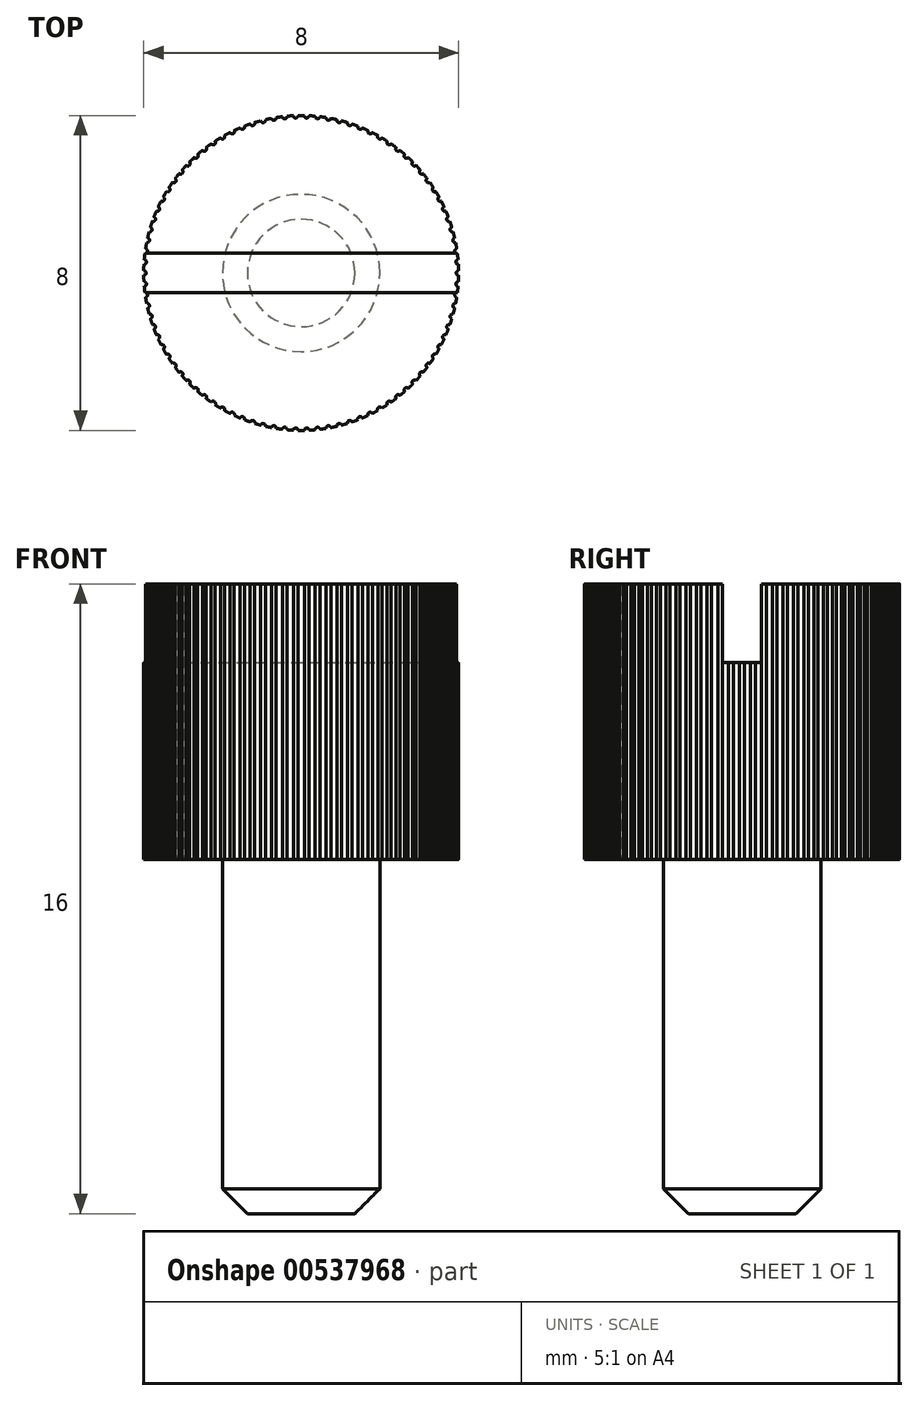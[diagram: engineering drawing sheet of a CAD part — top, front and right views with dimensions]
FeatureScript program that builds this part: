
annotation { "Feature Type Name" : "Feature", "Feature Type Description" : "" }
export const myFeature = defineFeature(function(context is Context, id is Id, definition is map)
    precondition{}
    {
        {
            var Q0;
            Q0=qCreatedBy(makeId("Top.planeOp"),FACE);
            var sketch = newSketch(context, id + "F0", { "sketchPlane" : qUnion([Q0])});
            skCircle(sketch, "E0", {"center": v(0, 0) * mm, "radius": 2 * mm});
            skSolve(sketch);
        }
        {
            var Q0;
            Q0=makeQuery(id+"F0.imprint","IMPRINT",FACE,{"disambiguationData":[TD([[makeQuery(id+"F0.imprint","IMPRINT",EDGE,{"derivedFrom":sQuery(id+"F0.wireOp",EDGE,"E0")}),1.0]])]});
            extrude(context, id + "F1", {"entities" : qUnion([Q0]), "oppositeDirection" : true, "depth" : 9 * mm, "offsetDistance" : 25 * mm});
        }
        {
            var Q0;
            Q0=qCreatedBy(makeId("Top.planeOp"),FACE);
            var sketch = newSketch(context, id + "F2", { "sketchPlane" : qUnion([Q0])});
            skCircle(sketch, "E1", {"center": v(0, 0) * mm, "radius": 4 * mm});
            skSolve(sketch);
        }
        {
            var Q0;
            Q0=makeQuery(id+"F2.imprint","IMPRINT",FACE,{"disambiguationData":[TD([[makeQuery(id+"F2.imprint","IMPRINT",EDGE,{"derivedFrom":sQuery(id+"F2.wireOp",EDGE,"E1")}),1.0]])]});
            extrude(context, id + "F3", {"entities" : qUnion([Q0]), "operationType" : NewBodyOperationType.ADD, "depth" : 7 * mm, "offsetDistance" : 25 * mm});
        }
        {
            var Q0;
            Q0=makeQuery(id+"F3.opExtrude","CAP_FACE",FACE,{"disambiguationData":[OSD([sQuery(id+"F2.wireOp",EDGE,"E1")])],"isStart":false});
            var sketch = newSketch(context, id + "F4", { "sketchPlane" : qUnion([Q0])});
            skLineSegment(sketch, "E2.bottom", {"start": v(-4.5, 0.5) * mm, "end": v(4.5, 0.5) * mm});
            skLineSegment(sketch, "E2.top", {"start": v(-4.5, -0.5) * mm, "end": v(4.5, -0.5) * mm});
            skLineSegment(sketch, "E2.left", {"start": v(-4.5, 0.5) * mm, "end": v(-4.5, -0.5) * mm});
            skLineSegment(sketch, "E2.right", {"start": v(4.5, 0.5) * mm, "end": v(4.5, -0.5) * mm});
            skPoint(sketch, "E2.middle", {"position": v(0, 0) * mm});
            skSolve(sketch);
        }
        {
            var Q0;
            Q0=qSketchRegion(id+"F4",true);
            extrude(context, id + "F5", {"entities" : qUnion([Q0]), "operationType" : NewBodyOperationType.REMOVE, "oppositeDirection" : true, "depth" : 2 * mm, "offsetDistance" : 25 * mm});
        }
        {
            var Q0;
            Q0=makeQuery(id+"F1.opExtrude","CAP_EDGE",EDGE,{"disambiguationData":[OSD([sQuery(id+"F0.wireOp",EDGE,"E0")])],"isStart":false});
            chamfer(context, id + "F6", {"entities" : qUnion([Q0]), "width" : .635 * mm, "tangentPropagation" : true});
        }
        {
            var Q0;
            Q0=makeQuery(id+"F3.opExtrude","CAP_FACE",FACE,{"disambiguationData":[OSD([sQuery(id+"F2.wireOp",EDGE,"E1")])],"isStart":true});
            var sketch = newSketch(context, id + "F7", { "sketchPlane" : qUnion([Q0])});
            skPoint(sketch, "E3", {"position": v(4, 0) * mm});
            skPoint(sketch, "E4.1.0", {"position": v(4, 0.28) * mm});
            skPoint(sketch, "E4.2.0", {"position": v(3.96, 0.56) * mm});
            skPoint(sketch, "E4.3.0", {"position": v(3.91, 0.83) * mm});
            skPoint(sketch, "E4.4.0", {"position": v(3.85, 1.1) * mm});
            skPoint(sketch, "E4.5.0", {"position": v(3.76, 1.37) * mm});
            skPoint(sketch, "E4.6.0", {"position": v(3.65, 1.63) * mm});
            skPoint(sketch, "E4.7.0", {"position": v(3.53, 1.88) * mm});
            skPoint(sketch, "E4.8.0", {"position": v(3.4, 2.12) * mm});
            skPoint(sketch, "E4.9.0", {"position": v(3.24, 2.35) * mm});
            skPoint(sketch, "E4.10.0", {"position": v(3.06, 2.57) * mm});
            skPoint(sketch, "E4.11.0", {"position": v(2.88, 2.78) * mm});
            skPoint(sketch, "E4.12.0", {"position": v(2.68, 2.97) * mm});
            skPoint(sketch, "E4.13.0", {"position": v(2.46, 3.15) * mm});
            skPoint(sketch, "E4.14.0", {"position": v(2.24, 3.32) * mm});
            skPoint(sketch, "E4.15.0", {"position": v(2, 3.46) * mm});
            skPoint(sketch, "E4.16.0", {"position": v(1.75, 3.6) * mm});
            skPoint(sketch, "E4.17.0", {"position": v(1.5, 3.7) * mm});
            skPoint(sketch, "E4.18.0", {"position": v(1.24, 3.8) * mm});
            skPoint(sketch, "E4.19.0", {"position": v(0.97, 3.88) * mm});
            skPoint(sketch, "E4.20.0", {"position": v(0.7, 3.94) * mm});
            skPoint(sketch, "E4.21.0", {"position": v(0.42, 3.98) * mm});
            skPoint(sketch, "E4.22.0", {"position": v(0.14, 4) * mm});
            skPoint(sketch, "E4.23.0", {"position": v(-0.14, 4) * mm});
            skPoint(sketch, "E4.24.0", {"position": v(-0.42, 3.98) * mm});
            skPoint(sketch, "E4.25.0", {"position": v(-0.7, 3.94) * mm});
            skPoint(sketch, "E4.26.0", {"position": v(-0.97, 3.88) * mm});
            skPoint(sketch, "E4.27.0", {"position": v(-1.24, 3.8) * mm});
            skPoint(sketch, "E4.28.0", {"position": v(-1.5, 3.7) * mm});
            skPoint(sketch, "E4.29.0", {"position": v(-1.75, 3.6) * mm});
            skPoint(sketch, "E4.30.0", {"position": v(-2, 3.46) * mm});
            skPoint(sketch, "E4.31.0", {"position": v(-2.24, 3.32) * mm});
            skPoint(sketch, "E4.32.0", {"position": v(-2.46, 3.15) * mm});
            skPoint(sketch, "E4.33.0", {"position": v(-2.68, 2.97) * mm});
            skPoint(sketch, "E4.34.0", {"position": v(-2.88, 2.78) * mm});
            skPoint(sketch, "E4.35.0", {"position": v(-3.06, 2.57) * mm});
            skPoint(sketch, "E4.36.0", {"position": v(-3.24, 2.35) * mm});
            skPoint(sketch, "E4.37.0", {"position": v(-3.4, 2.12) * mm});
            skPoint(sketch, "E4.38.0", {"position": v(-3.53, 1.88) * mm});
            skPoint(sketch, "E4.39.0", {"position": v(-3.65, 1.63) * mm});
            skPoint(sketch, "E4.40.0", {"position": v(-3.76, 1.37) * mm});
            skPoint(sketch, "E4.41.0", {"position": v(-3.85, 1.1) * mm});
            skPoint(sketch, "E4.42.0", {"position": v(-3.91, 0.83) * mm});
            skPoint(sketch, "E4.43.0", {"position": v(-3.96, 0.56) * mm});
            skPoint(sketch, "E4.44.0", {"position": v(-4, 0.28) * mm});
            skPoint(sketch, "E4.45.0", {"position": v(-4, 0) * mm});
            skPoint(sketch, "E4.46.0", {"position": v(-4, -0.28) * mm});
            skPoint(sketch, "E4.47.0", {"position": v(-3.96, -0.56) * mm});
            skPoint(sketch, "E4.48.0", {"position": v(-3.91, -0.83) * mm});
            skPoint(sketch, "E4.49.0", {"position": v(-3.85, -1.1) * mm});
            skPoint(sketch, "E4.50.0", {"position": v(-3.76, -1.37) * mm});
            skPoint(sketch, "E4.51.0", {"position": v(-3.65, -1.63) * mm});
            skPoint(sketch, "E4.52.0", {"position": v(-3.53, -1.88) * mm});
            skPoint(sketch, "E4.53.0", {"position": v(-3.4, -2.12) * mm});
            skPoint(sketch, "E4.54.0", {"position": v(-3.24, -2.35) * mm});
            skPoint(sketch, "E4.55.0", {"position": v(-3.06, -2.57) * mm});
            skPoint(sketch, "E4.56.0", {"position": v(-2.88, -2.78) * mm});
            skPoint(sketch, "E4.57.0", {"position": v(-2.68, -2.97) * mm});
            skPoint(sketch, "E4.58.0", {"position": v(-2.46, -3.15) * mm});
            skPoint(sketch, "E4.59.0", {"position": v(-2.24, -3.32) * mm});
            skPoint(sketch, "E4.60.0", {"position": v(-2, -3.46) * mm});
            skPoint(sketch, "E4.61.0", {"position": v(-1.75, -3.6) * mm});
            skPoint(sketch, "E4.62.0", {"position": v(-1.5, -3.7) * mm});
            skPoint(sketch, "E4.63.0", {"position": v(-1.24, -3.8) * mm});
            skPoint(sketch, "E4.64.0", {"position": v(-0.97, -3.88) * mm});
            skPoint(sketch, "E4.65.0", {"position": v(-0.7, -3.94) * mm});
            skPoint(sketch, "E4.66.0", {"position": v(-0.42, -3.98) * mm});
            skPoint(sketch, "E4.67.0", {"position": v(-0.14, -4) * mm});
            skPoint(sketch, "E4.68.0", {"position": v(0.14, -4) * mm});
            skPoint(sketch, "E4.69.0", {"position": v(0.42, -3.98) * mm});
            skPoint(sketch, "E4.70.0", {"position": v(0.7, -3.94) * mm});
            skPoint(sketch, "E4.71.0", {"position": v(0.97, -3.88) * mm});
            skPoint(sketch, "E4.72.0", {"position": v(1.24, -3.8) * mm});
            skPoint(sketch, "E4.73.0", {"position": v(1.5, -3.7) * mm});
            skPoint(sketch, "E4.74.0", {"position": v(1.75, -3.6) * mm});
            skPoint(sketch, "E4.75.0", {"position": v(2, -3.46) * mm});
            skPoint(sketch, "E4.76.0", {"position": v(2.24, -3.32) * mm});
            skPoint(sketch, "E4.77.0", {"position": v(2.46, -3.15) * mm});
            skPoint(sketch, "E4.78.0", {"position": v(2.68, -2.97) * mm});
            skPoint(sketch, "E4.79.0", {"position": v(2.88, -2.78) * mm});
            skPoint(sketch, "E4.80.0", {"position": v(3.06, -2.57) * mm});
            skPoint(sketch, "E4.81.0", {"position": v(3.24, -2.35) * mm});
            skPoint(sketch, "E4.82.0", {"position": v(3.4, -2.12) * mm});
            skPoint(sketch, "E4.83.0", {"position": v(3.53, -1.88) * mm});
            skPoint(sketch, "E4.84.0", {"position": v(3.65, -1.63) * mm});
            skPoint(sketch, "E4.85.0", {"position": v(3.76, -1.37) * mm});
            skPoint(sketch, "E4.86.0", {"position": v(3.85, -1.1) * mm});
            skPoint(sketch, "E4.87.0", {"position": v(3.91, -0.83) * mm});
            skPoint(sketch, "E4.88.0", {"position": v(3.96, -0.56) * mm});
            skPoint(sketch, "E4.89.0", {"position": v(4, -0.28) * mm});
            skPoint(sketch, "E4.center", {"position": v(0, 0) * mm});
            skSolve(sketch);
        }
        {
            var Q0;
            Q0=sQuery(id+"F7.wireOp",VERTEX,"E3");
            var Q1;
            Q1=sQuery(id+"F7.wireOp",VERTEX,"88757db8-3b25-47bd-b450-de60e4cef4e0.0.179.0");
            var Q2;
            Q2=sQuery(id+"F7.wireOp",VERTEX,"88757db8-3b25-47bd-b450-de60e4cef4e0.0.165.0");
            var Q3;
            Q3=sQuery(id+"F7.wireOp",VERTEX,"88757db8-3b25-47bd-b450-de60e4cef4e0.0.174.0");
            var Q4;
            Q4=sQuery(id+"F7.wireOp",VERTEX,"88757db8-3b25-47bd-b450-de60e4cef4e0.0.168.0");
            var Q5;
            Q5=sQuery(id+"F7.wireOp",VERTEX,"88757db8-3b25-47bd-b450-de60e4cef4e0.0.171.0");
            var Q6;
            Q6=sQuery(id+"F7.wireOp",VERTEX,"88757db8-3b25-47bd-b450-de60e4cef4e0.0.164.0");
            var Q7;
            Q7=sQuery(id+"F7.wireOp",VERTEX,"88757db8-3b25-47bd-b450-de60e4cef4e0.0.167.0");
            var Q8;
            Q8=sQuery(id+"F7.wireOp",VERTEX,"88757db8-3b25-47bd-b450-de60e4cef4e0.0.177.0");
            var Q9;
            Q9=sQuery(id+"F7.wireOp",VERTEX,"88757db8-3b25-47bd-b450-de60e4cef4e0.0.169.0");
            var Q10;
            Q10=sQuery(id+"F7.wireOp",VERTEX,"88757db8-3b25-47bd-b450-de60e4cef4e0.0.178.0");
            var Q11;
            Q11=sQuery(id+"F7.wireOp",VERTEX,"88757db8-3b25-47bd-b450-de60e4cef4e0.0.166.0");
            var Q12;
            Q12=sQuery(id+"F7.wireOp",VERTEX,"88757db8-3b25-47bd-b450-de60e4cef4e0.0.172.0");
            var Q13;
            Q13=sQuery(id+"F7.wireOp",VERTEX,"88757db8-3b25-47bd-b450-de60e4cef4e0.0.163.0");
            var Q14;
            Q14=sQuery(id+"F7.wireOp",VERTEX,"88757db8-3b25-47bd-b450-de60e4cef4e0.0.175.0");
            var Q15;
            Q15=sQuery(id+"F7.wireOp",VERTEX,"88757db8-3b25-47bd-b450-de60e4cef4e0.0.170.0");
            var Q16;
            Q16=sQuery(id+"F7.wireOp",VERTEX,"88757db8-3b25-47bd-b450-de60e4cef4e0.0.176.0");
            var Q17;
            Q17=sQuery(id+"F7.wireOp",VERTEX,"88757db8-3b25-47bd-b450-de60e4cef4e0.0.173.0");
            var Q18;
            Q18=sQuery(id+"F7.wireOp",VERTEX,"88757db8-3b25-47bd-b450-de60e4cef4e0.0.158.0");
            var Q19;
            Q19=sQuery(id+"F7.wireOp",VERTEX,"88757db8-3b25-47bd-b450-de60e4cef4e0.0.160.0");
            var Q20;
            Q20=sQuery(id+"F7.wireOp",VERTEX,"88757db8-3b25-47bd-b450-de60e4cef4e0.0.157.0");
            var Q21;
            Q21=sQuery(id+"F7.wireOp",VERTEX,"88757db8-3b25-47bd-b450-de60e4cef4e0.0.161.0");
            var Q22;
            Q22=sQuery(id+"F7.wireOp",VERTEX,"88757db8-3b25-47bd-b450-de60e4cef4e0.0.162.0");
            var Q23;
            Q23=sQuery(id+"F7.wireOp",VERTEX,"88757db8-3b25-47bd-b450-de60e4cef4e0.0.159.0");
            var Q24;
            Q24=sQuery(id+"F7.wireOp",VERTEX,"88757db8-3b25-47bd-b450-de60e4cef4e0.0.152.0");
            var Q25;
            Q25=sQuery(id+"F7.wireOp",VERTEX,"88757db8-3b25-47bd-b450-de60e4cef4e0.0.149.0");
            var Q26;
            Q26=sQuery(id+"F7.wireOp",VERTEX,"88757db8-3b25-47bd-b450-de60e4cef4e0.0.155.0");
            var Q27;
            Q27=sQuery(id+"F7.wireOp",VERTEX,"88757db8-3b25-47bd-b450-de60e4cef4e0.0.148.0");
            var Q28;
            Q28=sQuery(id+"F7.wireOp",VERTEX,"88757db8-3b25-47bd-b450-de60e4cef4e0.0.151.0");
            var Q29;
            Q29=sQuery(id+"F7.wireOp",VERTEX,"88757db8-3b25-47bd-b450-de60e4cef4e0.0.145.0");
            var Q30;
            Q30=sQuery(id+"F7.wireOp",VERTEX,"88757db8-3b25-47bd-b450-de60e4cef4e0.0.153.0");
            var Q31;
            Q31=sQuery(id+"F7.wireOp",VERTEX,"88757db8-3b25-47bd-b450-de60e4cef4e0.0.150.0");
            var Q32;
            Q32=sQuery(id+"F7.wireOp",VERTEX,"88757db8-3b25-47bd-b450-de60e4cef4e0.0.156.0");
            var Q33;
            Q33=sQuery(id+"F7.wireOp",VERTEX,"88757db8-3b25-47bd-b450-de60e4cef4e0.0.147.0");
            var Q34;
            Q34=sQuery(id+"F7.wireOp",VERTEX,"88757db8-3b25-47bd-b450-de60e4cef4e0.0.154.0");
            var Q35;
            Q35=sQuery(id+"F7.wireOp",VERTEX,"88757db8-3b25-47bd-b450-de60e4cef4e0.0.117.0");
            var Q36;
            Q36=sQuery(id+"F7.wireOp",VERTEX,"88757db8-3b25-47bd-b450-de60e4cef4e0.0.120.0");
            var Q37;
            Q37=sQuery(id+"F7.wireOp",VERTEX,"88757db8-3b25-47bd-b450-de60e4cef4e0.0.104.0");
            var Q38;
            Q38=sQuery(id+"F7.wireOp",VERTEX,"88757db8-3b25-47bd-b450-de60e4cef4e0.0.110.0");
            var Q39;
            Q39=sQuery(id+"F7.wireOp",VERTEX,"88757db8-3b25-47bd-b450-de60e4cef4e0.0.142.0");
            var Q40;
            Q40=sQuery(id+"F7.wireOp",VERTEX,"88757db8-3b25-47bd-b450-de60e4cef4e0.0.103.0");
            var Q41;
            Q41=sQuery(id+"F7.wireOp",VERTEX,"88757db8-3b25-47bd-b450-de60e4cef4e0.0.126.0");
            var Q42;
            Q42=sQuery(id+"F7.wireOp",VERTEX,"88757db8-3b25-47bd-b450-de60e4cef4e0.0.139.0");
            var Q43;
            Q43=sQuery(id+"F7.wireOp",VERTEX,"88757db8-3b25-47bd-b450-de60e4cef4e0.0.141.0");
            var Q44;
            Q44=sQuery(id+"F7.wireOp",VERTEX,"88757db8-3b25-47bd-b450-de60e4cef4e0.0.107.0");
            var Q45;
            Q45=sQuery(id+"F7.wireOp",VERTEX,"88757db8-3b25-47bd-b450-de60e4cef4e0.0.144.0");
            var Q46;
            Q46=sQuery(id+"F7.wireOp",VERTEX,"88757db8-3b25-47bd-b450-de60e4cef4e0.0.112.0");
            var Q47;
            Q47=sQuery(id+"F7.wireOp",VERTEX,"88757db8-3b25-47bd-b450-de60e4cef4e0.0.109.0");
            var Q48;
            Q48=sQuery(id+"F7.wireOp",VERTEX,"88757db8-3b25-47bd-b450-de60e4cef4e0.0.116.0");
            var Q49;
            Q49=sQuery(id+"F7.wireOp",VERTEX,"88757db8-3b25-47bd-b450-de60e4cef4e0.0.119.0");
            var Q50;
            Q50=sQuery(id+"F7.wireOp",VERTEX,"88757db8-3b25-47bd-b450-de60e4cef4e0.0.113.0");
            var Q51;
            Q51=sQuery(id+"F7.wireOp",VERTEX,"88757db8-3b25-47bd-b450-de60e4cef4e0.0.130.0");
            var Q52;
            Q52=sQuery(id+"F7.wireOp",VERTEX,"88757db8-3b25-47bd-b450-de60e4cef4e0.0.114.0");
            var Q53;
            Q53=sQuery(id+"F7.wireOp",VERTEX,"88757db8-3b25-47bd-b450-de60e4cef4e0.0.146.0");
            var Q54;
            Q54=sQuery(id+"F7.wireOp",VERTEX,"88757db8-3b25-47bd-b450-de60e4cef4e0.0.105.0");
            var Q55;
            Q55=sQuery(id+"F7.wireOp",VERTEX,"88757db8-3b25-47bd-b450-de60e4cef4e0.0.131.0");
            var Q56;
            Q56=sQuery(id+"F7.wireOp",VERTEX,"88757db8-3b25-47bd-b450-de60e4cef4e0.0.124.0");
            var Q57;
            Q57=sQuery(id+"F7.wireOp",VERTEX,"88757db8-3b25-47bd-b450-de60e4cef4e0.0.115.0");
            var Q58;
            Q58=sQuery(id+"F7.wireOp",VERTEX,"88757db8-3b25-47bd-b450-de60e4cef4e0.0.108.0");
            var Q59;
            Q59=sQuery(id+"F7.wireOp",VERTEX,"88757db8-3b25-47bd-b450-de60e4cef4e0.0.102.0");
            var Q60;
            Q60=sQuery(id+"F7.wireOp",VERTEX,"88757db8-3b25-47bd-b450-de60e4cef4e0.0.134.0");
            var Q61;
            Q61=sQuery(id+"F7.wireOp",VERTEX,"88757db8-3b25-47bd-b450-de60e4cef4e0.0.118.0");
            var Q62;
            Q62=sQuery(id+"F7.wireOp",VERTEX,"88757db8-3b25-47bd-b450-de60e4cef4e0.0.140.0");
            var Q63;
            Q63=sQuery(id+"F7.wireOp",VERTEX,"88757db8-3b25-47bd-b450-de60e4cef4e0.0.127.0");
            var Q64;
            Q64=sQuery(id+"F7.wireOp",VERTEX,"88757db8-3b25-47bd-b450-de60e4cef4e0.0.111.0");
            var Q65;
            Q65=sQuery(id+"F7.wireOp",VERTEX,"88757db8-3b25-47bd-b450-de60e4cef4e0.0.143.0");
            var Q66;
            Q66=sQuery(id+"F7.wireOp",VERTEX,"88757db8-3b25-47bd-b450-de60e4cef4e0.0.106.0");
            var Q67;
            Q67=sQuery(id+"F7.wireOp",VERTEX,"88757db8-3b25-47bd-b450-de60e4cef4e0.0.138.0");
            var Q68;
            Q68=sQuery(id+"F7.wireOp",VERTEX,"88757db8-3b25-47bd-b450-de60e4cef4e0.0.133.0");
            var Q69;
            Q69=sQuery(id+"F7.wireOp",VERTEX,"88757db8-3b25-47bd-b450-de60e4cef4e0.0.128.0");
            var Q70;
            Q70=sQuery(id+"F7.wireOp",VERTEX,"88757db8-3b25-47bd-b450-de60e4cef4e0.0.125.0");
            var Q71;
            Q71=sQuery(id+"F7.wireOp",VERTEX,"88757db8-3b25-47bd-b450-de60e4cef4e0.0.132.0");
            var Q72;
            Q72=sQuery(id+"F7.wireOp",VERTEX,"88757db8-3b25-47bd-b450-de60e4cef4e0.0.129.0");
            var Q73;
            Q73=sQuery(id+"F7.wireOp",VERTEX,"88757db8-3b25-47bd-b450-de60e4cef4e0.0.136.0");
            var Q74;
            Q74=sQuery(id+"F7.wireOp",VERTEX,"88757db8-3b25-47bd-b450-de60e4cef4e0.0.123.0");
            var Q75;
            Q75=sQuery(id+"F7.wireOp",VERTEX,"88757db8-3b25-47bd-b450-de60e4cef4e0.0.135.0");
            var Q76;
            Q76=sQuery(id+"F7.wireOp",VERTEX,"88757db8-3b25-47bd-b450-de60e4cef4e0.0.137.0");
            var Q77;
            Q77=sQuery(id+"F7.wireOp",VERTEX,"88757db8-3b25-47bd-b450-de60e4cef4e0.0.121.0");
            var Q78;
            Q78=sQuery(id+"F7.wireOp",VERTEX,"88757db8-3b25-47bd-b450-de60e4cef4e0.0.122.0");
            var Q79;
            Q79=sQuery(id+"F7.wireOp",VERTEX,"E4.24.0");
            var Q80;
            Q80=sQuery(id+"F7.wireOp",VERTEX,"E4.22.0");
            var Q81;
            Q81=sQuery(id+"F7.wireOp",VERTEX,"E4.31.0");
            var Q82;
            Q82=sQuery(id+"F7.wireOp",VERTEX,"E4.47.0");
            var Q83;
            Q83=sQuery(id+"F7.wireOp",VERTEX,"E4.12.0");
            var Q84;
            Q84=sQuery(id+"F7.wireOp",VERTEX,"E4.11.0");
            var Q85;
            Q85=sQuery(id+"F7.wireOp",VERTEX,"E4.10.0");
            var Q86;
            Q86=sQuery(id+"F7.wireOp",VERTEX,"E4.9.0");
            var Q87;
            Q87=sQuery(id+"F7.wireOp",VERTEX,"E4.28.0");
            var Q88;
            Q88=sQuery(id+"F7.wireOp",VERTEX,"E4.17.0");
            var Q89;
            Q89=sQuery(id+"F7.wireOp",VERTEX,"E4.7.0");
            var Q90;
            Q90=sQuery(id+"F7.wireOp",VERTEX,"E4.49.0");
            var Q91;
            Q91=sQuery(id+"F7.wireOp",VERTEX,"E4.21.0");
            var Q92;
            Q92=sQuery(id+"F7.wireOp",VERTEX,"E4.18.0");
            var Q93;
            Q93=sQuery(id+"F7.wireOp",VERTEX,"E4.19.0");
            var Q94;
            Q94=sQuery(id+"F7.wireOp",VERTEX,"E4.29.0");
            var Q95;
            Q95=sQuery(id+"F7.wireOp",VERTEX,"E4.20.0");
            var Q96;
            Q96=sQuery(id+"F7.wireOp",VERTEX,"E4.23.0");
            var Q97;
            Q97=sQuery(id+"F7.wireOp",VERTEX,"E4.13.0");
            var Q98;
            Q98=sQuery(id+"F7.wireOp",VERTEX,"E4.48.0");
            var Q99;
            Q99=sQuery(id+"F7.wireOp",VERTEX,"E4.16.0");
            var Q100;
            Q100=sQuery(id+"F7.wireOp",VERTEX,"E4.14.0");
            var Q101;
            Q101=sQuery(id+"F7.wireOp",VERTEX,"E4.15.0");
            var Q102;
            Q102=sQuery(id+"F7.wireOp",VERTEX,"E4.27.0");
            var Q103;
            Q103=sQuery(id+"F7.wireOp",VERTEX,"E4.30.0");
            var Q104;
            Q104=sQuery(id+"F7.wireOp",VERTEX,"E4.8.0");
            var Q105;
            Q105=sQuery(id+"F7.wireOp",VERTEX,"E4.6.0");
            var Q106;
            Q106=sQuery(id+"F7.wireOp",VERTEX,"E4.5.0");
            var Q107;
            Q107=sQuery(id+"F7.wireOp",VERTEX,"E4.4.0");
            var Q108;
            Q108=sQuery(id+"F7.wireOp",VERTEX,"E4.3.0");
            var Q109;
            Q109=sQuery(id+"F7.wireOp",VERTEX,"E4.2.0");
            var Q110;
            Q110=sQuery(id+"F7.wireOp",VERTEX,"E4.1.0");
            var Q111;
            Q111=sQuery(id+"F7.wireOp",VERTEX,"E4.72.0");
            var Q112;
            Q112=sQuery(id+"F7.wireOp",VERTEX,"E4.89.0");
            var Q113;
            Q113=sQuery(id+"F7.wireOp",VERTEX,"E4.73.0");
            var Q114;
            Q114=sQuery(id+"F7.wireOp",VERTEX,"88757db8-3b25-47bd-b450-de60e4cef4e0.0.94.0");
            var Q115;
            Q115=sQuery(id+"F7.wireOp",VERTEX,"E4.88.0");
            var Q116;
            Q116=sQuery(id+"F7.wireOp",VERTEX,"E4.66.0");
            var Q117;
            Q117=sQuery(id+"F7.wireOp",VERTEX,"E4.79.0");
            var Q118;
            Q118=sQuery(id+"F7.wireOp",VERTEX,"E4.70.0");
            var Q119;
            Q119=sQuery(id+"F7.wireOp",VERTEX,"E4.76.0");
            var Q120;
            Q120=sQuery(id+"F7.wireOp",VERTEX,"88757db8-3b25-47bd-b450-de60e4cef4e0.0.91.0");
            var Q121;
            Q121=sQuery(id+"F7.wireOp",VERTEX,"E4.81.0");
            var Q122;
            Q122=sQuery(id+"F7.wireOp",VERTEX,"88757db8-3b25-47bd-b450-de60e4cef4e0.0.96.0");
            var Q123;
            Q123=sQuery(id+"F7.wireOp",VERTEX,"E4.78.0");
            var Q124;
            Q124=sQuery(id+"F7.wireOp",VERTEX,"88757db8-3b25-47bd-b450-de60e4cef4e0.0.93.0");
            var Q125;
            Q125=sQuery(id+"F7.wireOp",VERTEX,"88757db8-3b25-47bd-b450-de60e4cef4e0.0.100.0");
            var Q126;
            Q126=sQuery(id+"F7.wireOp",VERTEX,"E4.69.0");
            var Q127;
            Q127=sQuery(id+"F7.wireOp",VERTEX,"88757db8-3b25-47bd-b450-de60e4cef4e0.0.97.0");
            var Q128;
            Q128=sQuery(id+"F7.wireOp",VERTEX,"E4.82.0");
            var Q129;
            Q129=sQuery(id+"F7.wireOp",VERTEX,"E4.67.0");
            var Q130;
            Q130=sQuery(id+"F7.wireOp",VERTEX,"88757db8-3b25-47bd-b450-de60e4cef4e0.0.98.0");
            var Q131;
            Q131=sQuery(id+"F7.wireOp",VERTEX,"E4.83.0");
            var Q132;
            Q132=sQuery(id+"F7.wireOp",VERTEX,"E4.74.0");
            var Q133;
            Q133=sQuery(id+"F7.wireOp",VERTEX,"E4.68.0");
            var Q134;
            Q134=sQuery(id+"F7.wireOp",VERTEX,"88757db8-3b25-47bd-b450-de60e4cef4e0.0.92.0");
            var Q135;
            Q135=sQuery(id+"F7.wireOp",VERTEX,"88757db8-3b25-47bd-b450-de60e4cef4e0.0.99.0");
            var Q136;
            Q136=sQuery(id+"F7.wireOp",VERTEX,"E4.77.0");
            var Q137;
            Q137=sQuery(id+"F7.wireOp",VERTEX,"E4.84.0");
            var Q138;
            Q138=sQuery(id+"F7.wireOp",VERTEX,"E4.87.0");
            var Q139;
            Q139=sQuery(id+"F7.wireOp",VERTEX,"E4.71.0");
            var Q140;
            Q140=sQuery(id+"F7.wireOp",VERTEX,"E4.64.0");
            var Q141;
            Q141=sQuery(id+"F7.wireOp",VERTEX,"88757db8-3b25-47bd-b450-de60e4cef4e0.0.95.0");
            var Q142;
            Q142=sQuery(id+"F7.wireOp",VERTEX,"E4.80.0");
            var Q143;
            Q143=sQuery(id+"F7.wireOp",VERTEX,"88757db8-3b25-47bd-b450-de60e4cef4e0.0.90.0");
            var Q144;
            Q144=sQuery(id+"F7.wireOp",VERTEX,"E4.75.0");
            var Q145;
            Q145=sQuery(id+"F7.wireOp",VERTEX,"E4.86.0");
            var Q146;
            Q146=sQuery(id+"F7.wireOp",VERTEX,"E4.85.0");
            var Q147;
            Q147=sQuery(id+"F7.wireOp",VERTEX,"88757db8-3b25-47bd-b450-de60e4cef4e0.0.101.0");
            var Q148;
            Q148=sQuery(id+"F7.wireOp",VERTEX,"E4.57.0");
            var Q149;
            Q149=sQuery(id+"F7.wireOp",VERTEX,"E4.54.0");
            var Q150;
            Q150=sQuery(id+"F7.wireOp",VERTEX,"E4.60.0");
            var Q151;
            Q151=sQuery(id+"F7.wireOp",VERTEX,"E4.53.0");
            var Q152;
            Q152=sQuery(id+"F7.wireOp",VERTEX,"E4.56.0");
            var Q153;
            Q153=sQuery(id+"F7.wireOp",VERTEX,"E4.50.0");
            var Q154;
            Q154=sQuery(id+"F7.wireOp",VERTEX,"E4.51.0");
            var Q155;
            Q155=sQuery(id+"F7.wireOp",VERTEX,"E4.58.0");
            var Q156;
            Q156=sQuery(id+"F7.wireOp",VERTEX,"E4.45.0");
            var Q157;
            Q157=sQuery(id+"F7.wireOp",VERTEX,"E4.52.0");
            var Q158;
            Q158=sQuery(id+"F7.wireOp",VERTEX,"E4.55.0");
            var Q159;
            Q159=sQuery(id+"F7.wireOp",VERTEX,"E4.46.0");
            var Q160;
            Q160=sQuery(id+"F7.wireOp",VERTEX,"E4.63.0");
            var Q161;
            Q161=sQuery(id+"F7.wireOp",VERTEX,"E4.62.0");
            var Q162;
            Q162=sQuery(id+"F7.wireOp",VERTEX,"E4.61.0");
            var Q163;
            Q163=sQuery(id+"F7.wireOp",VERTEX,"E4.59.0");
            var Q164;
            Q164=sQuery(id+"F7.wireOp",VERTEX,"E4.65.0");
            var Q165;
            Q165=sQuery(id+"F7.wireOp",VERTEX,"E4.40.0");
            var Q166;
            Q166=sQuery(id+"F7.wireOp",VERTEX,"E4.44.0");
            var Q167;
            Q167=sQuery(id+"F7.wireOp",VERTEX,"E4.41.0");
            var Q168;
            Q168=sQuery(id+"F7.wireOp",VERTEX,"E4.25.0");
            var Q169;
            Q169=sQuery(id+"F7.wireOp",VERTEX,"E4.35.0");
            var Q170;
            Q170=sQuery(id+"F7.wireOp",VERTEX,"E4.42.0");
            var Q171;
            Q171=sQuery(id+"F7.wireOp",VERTEX,"E4.26.0");
            var Q172;
            Q172=sQuery(id+"F7.wireOp",VERTEX,"E4.36.0");
            var Q173;
            Q173=sQuery(id+"F7.wireOp",VERTEX,"E4.39.0");
            var Q174;
            Q174=sQuery(id+"F7.wireOp",VERTEX,"E4.32.0");
            var Q175;
            Q175=sQuery(id+"F7.wireOp",VERTEX,"E4.43.0");
            var Q176;
            Q176=sQuery(id+"F7.wireOp",VERTEX,"E4.38.0");
            var Q177;
            Q177=sQuery(id+"F7.wireOp",VERTEX,"E4.33.0");
            var Q178;
            Q178=sQuery(id+"F7.wireOp",VERTEX,"E4.37.0");
            var Q179;
            Q179=sQuery(id+"F7.wireOp",VERTEX,"E4.34.0");
            var Q180;
            Q180=makeQuery(id+"F1.opExtrude","SWEPT_BODY",BODY,{"disambiguationData":[OSD([sQuery(id+"F0.wireOp",EDGE,"E0")])]});
            hole(context, id + "F8", {"style" : HoleStyle.SIMPLE, "endStyle" : HoleEndStyle.THROUGH, "holeDiameter" : .12 * mm, "isTappedThrough" : true, "tappedDepth" : 12 * mm, "tapClearance" : 3, "locations" : qUnion([Q0, Q1, Q2, Q3, Q4, Q5, Q6, Q7, Q8, Q9, Q10, Q11, Q12, Q13, Q14, Q15, Q16, Q17, Q18, Q19, Q20, Q21, Q22, Q23, Q24, Q25, Q26, Q27, Q28, Q29, Q30, Q31, Q32, Q33, Q34, Q35, Q36, Q37, Q38, Q39, Q40, Q41, Q42, Q43, Q44, Q45, Q46, Q47, Q48, Q49, Q50, Q51, Q52, Q53, Q54, Q55, Q56, Q57, Q58, Q59, Q60, Q61, Q62, Q63, Q64, Q65, Q66, Q67, Q68, Q69, Q70, Q71, Q72, Q73, Q74, Q75, Q76, Q77, Q78, Q79, Q80, Q81, Q82, Q83, Q84, Q85, Q86, Q87, Q88, Q89, Q90, Q91, Q92, Q93, Q94, Q95, Q96, Q97, Q98, Q99, Q100, Q101, Q102, Q103, Q104, Q105, Q106, Q107, Q108, Q109, Q110, Q111, Q112, Q113, Q114, Q115, Q116, Q117, Q118, Q119, Q120, Q121, Q122, Q123, Q124, Q125, Q126, Q127, Q128, Q129, Q130, Q131, Q132, Q133, Q134, Q135, Q136, Q137, Q138, Q139, Q140, Q141, Q142, Q143, Q144, Q145, Q146, Q147, Q148, Q149, Q150, Q151, Q152, Q153, Q154, Q155, Q156, Q157, Q158, Q159, Q160, Q161, Q162, Q163, Q164, Q165, Q166, Q167, Q168, Q169, Q170, Q171, Q172, Q173, Q174, Q175, Q176, Q177, Q178, Q179]), "scope" : qUnion([Q180])});
        }
    });
